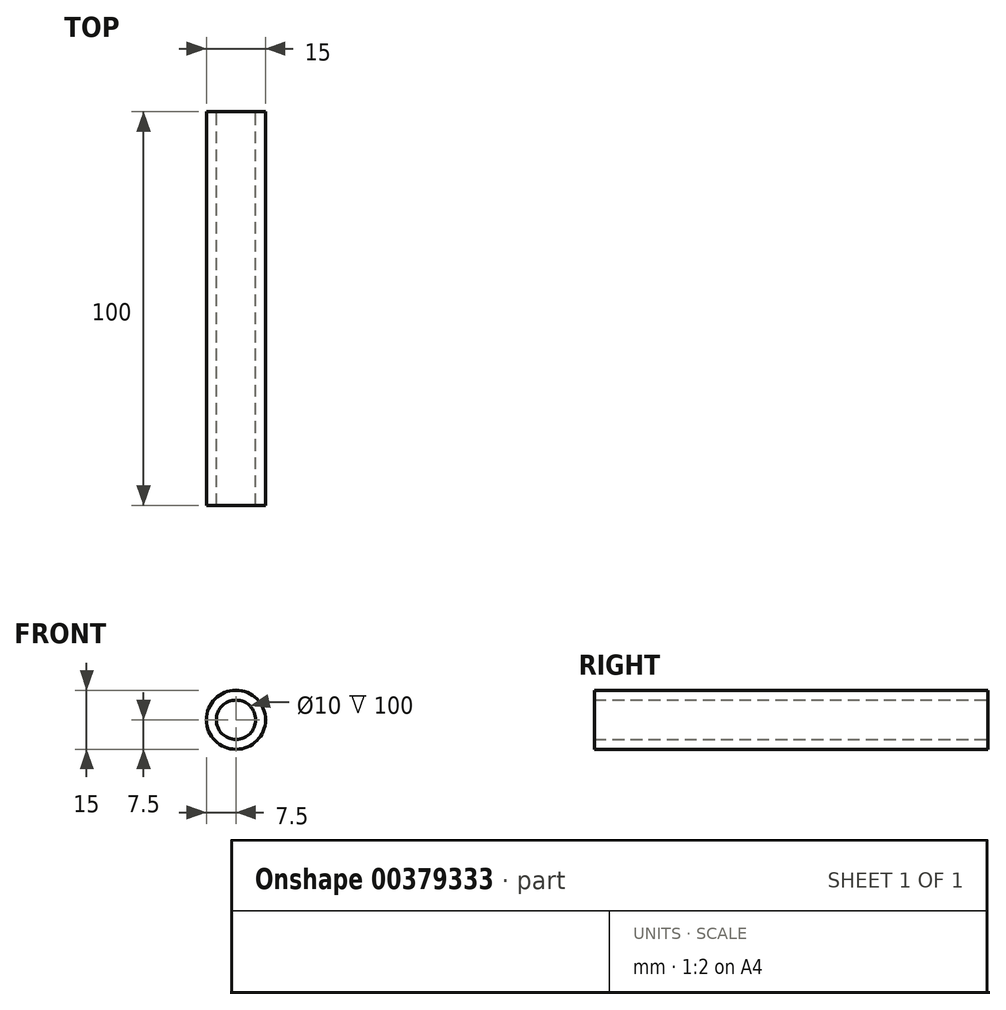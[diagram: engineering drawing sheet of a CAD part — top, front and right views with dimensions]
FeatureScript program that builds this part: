
annotation { "Feature Type Name" : "Feature", "Feature Type Description" : "" }
export const myFeature = defineFeature(function(context is Context, id is Id, definition is map)
    precondition{}
    {
        {
            var Q0;
            Q0=qCreatedBy(makeId("Front.planeOp"),FACE);
            var sketch = newSketch(context, id + "F0", { "sketchPlane" : qUnion([Q0])});
            skCircle(sketch, "E0", {"center": v(0, 0) * mm, "radius": 7.5 * mm});
            skCircle(sketch, "E1", {"center": v(0, 0) * mm, "radius": 5 * mm});
            skSolve(sketch);
        }
        {
            var Q0;
            Q0 = qSketchRegion(id + "F0", true);
            extrude(context, id + "F1", {"entities" : qUnion([Q0]), "depth" : 100 * mm});
        }
    });
